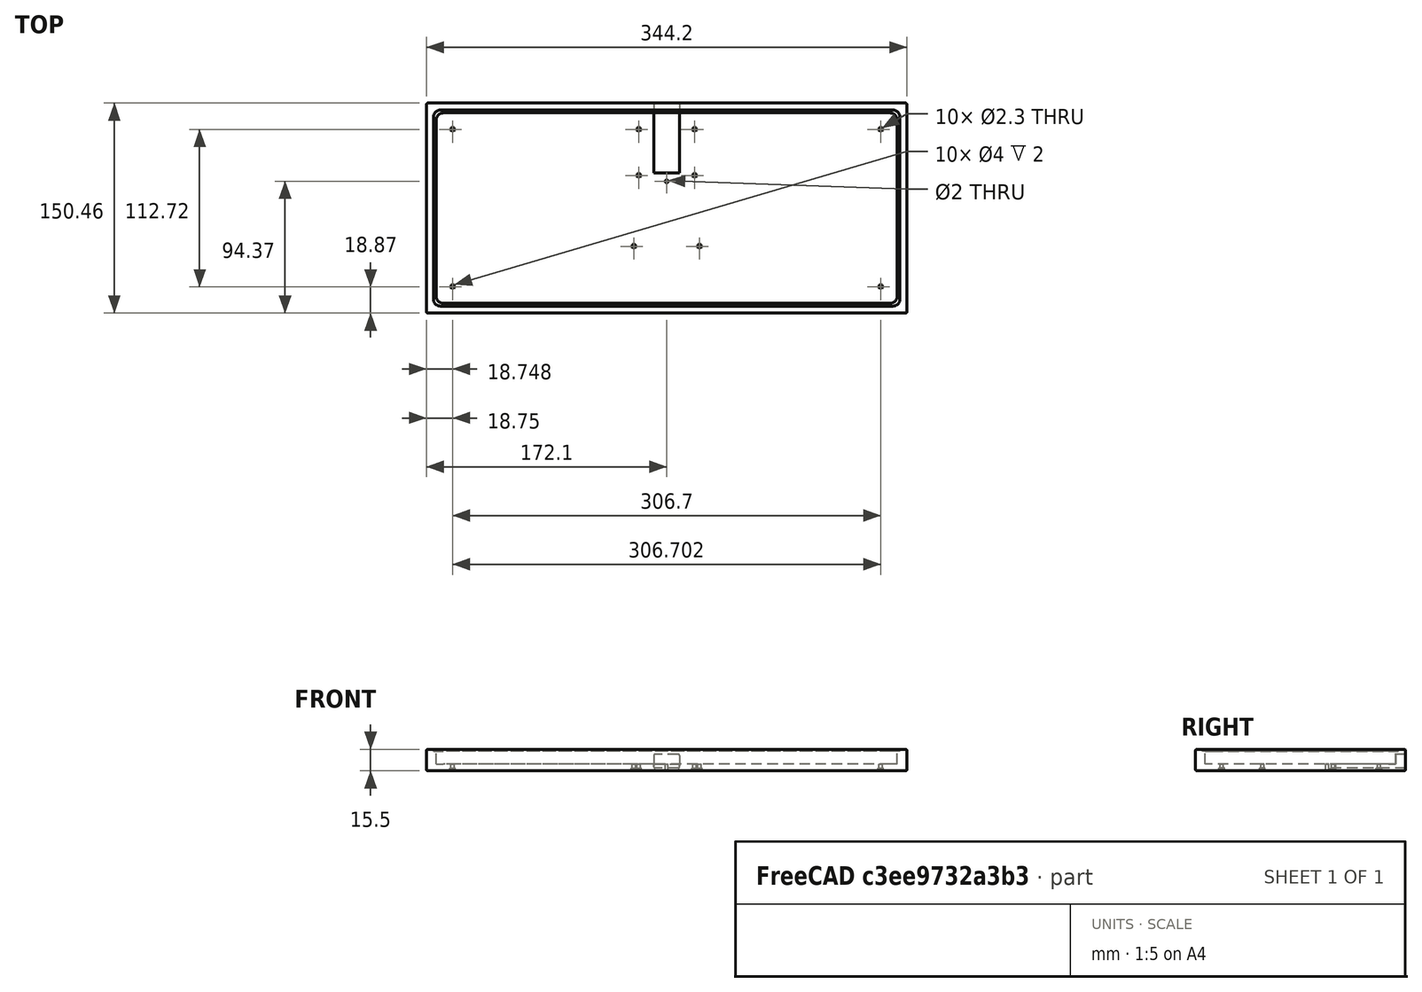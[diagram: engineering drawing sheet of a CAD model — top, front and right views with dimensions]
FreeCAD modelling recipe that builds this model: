
FCSTD DOCUMENT  (FreeCAD 0.18.1R)
Label: bloomer_case
License: All rights reserved
LicenseURL: http://en.wikipedia.org/wiki/All_rights_reserved
objects: Part::Cylinder×21, Part::Cut×6, Part::Box×4, Part::Fillet×4, Part::MultiFuse×2
note: 37 computed .brp shape members not serialized (recipe doc carries the construction recipe); baked Part::Feature solids carry a one-line shape summary decoded from their .brp

FEATURE [Part::Box] Box  label="Cube"
  AttacherType = Attacher::AttachEngine3D
  Height = 10.5
  Length = 330.204
  Placement = pos=(-165.102,-68.23,5) rot=(0,0,1;0rad)
  Width = 136.47
FEATURE [Part::Box] Box001  label="Cube001"
  AttacherType = Attacher::AttachEngine3D
  Height = 1.5
  Length = 334.204
  Placement = pos=(-167.1,-70.23,14) rot=(0,0,1;0rad)
  Width = 140.47
FEATURE [Part::Box] Box002  label="Cube002"
  AttacherType = Attacher::AttachEngine3D
  Height = 15.5
  Length = 344.204
  Placement = pos=(-172.102,-75.235,0) rot=(0,0,1;0rad)
  Width = 150.47
FEATURE [Part::Fillet] Fillet
  Base = -> Box
  Edges = 4 edges r=5: [Edge1,Edge3,Edge5,Edge7]
FEATURE [Part::Fillet] Fillet001
  Base = -> Box001
  Edges = 4 edges r=5: [Edge1,Edge3,Edge5,Edge7]
FEATURE [Part::Cut] Cut
  Base = -> Box002
  Tool = -> Fillet
FEATURE [Part::Cut] Cut001
  Base = -> Cut
  Tool = -> Fillet001
FEATURE [Part::Cylinder] Cylinder
  Angle = 360
  AttacherType = Attacher::AttachEngine3D
  Height = 5
  Placement = pos=(153.35,56.36,0) rot=(0,0,1;0rad)
  Radius = 1.15
FEATURE [Part::Cylinder] Cylinder001
  Angle = 360
  AttacherType = Attacher::AttachEngine3D
  Height = 5
  Placement = pos=(153.35,-56.36,0) rot=(0,0,1;0rad)
  Radius = 1.15
FEATURE [Part::Cylinder] Cylinder002
  Angle = 360
  AttacherType = Attacher::AttachEngine3D
  Height = 5
  Placement = pos=(-153.35,56.36,0) rot=(0,0,1;0rad)
  Radius = 1.15
FEATURE [Part::Cylinder] Cylinder003
  Angle = 360
  AttacherType = Attacher::AttachEngine3D
  Height = 5
  Placement = pos=(-153.35,-56.36,0) rot=(0,0,1;0rad)
  Radius = 1.15
FEATURE [Part::Cylinder] Cylinder004
  Angle = 360
  AttacherType = Attacher::AttachEngine3D
  Height = 5
  Placement = pos=(-20,-56.36,0) rot=(0,0,1;0rad)
  Radius = 1.15
FEATURE [Part::Cylinder] Cylinder005
  Angle = 360
  AttacherType = Attacher::AttachEngine3D
  Height = 5
  Placement = pos=(20,-56.36,0) rot=(0,0,1;0rad)
  Radius = 1.15
FEATURE [Part::Cylinder] Cylinder006
  Angle = 360
  AttacherType = Attacher::AttachEngine3D
  Height = 5
  Placement = pos=(-20,-23.36,0) rot=(0,0,1;0rad)
  Radius = 1.15
FEATURE [Part::Cylinder] Cylinder007
  Angle = 360
  AttacherType = Attacher::AttachEngine3D
  Height = 5
  Placement = pos=(20,-23.36,0) rot=(0,0,1;0rad)
  Radius = 1.15
FEATURE [Part::Cylinder] Cylinder008
  Angle = 360
  AttacherType = Attacher::AttachEngine3D
  Height = 5
  Placement = pos=(-23.5,27.36,0) rot=(0,0,1;0rad)
  Radius = 1.15
FEATURE [Part::Cylinder] Cylinder009
  Angle = 360
  AttacherType = Attacher::AttachEngine3D
  Height = 5
  Placement = pos=(23.5,27.36,0) rot=(0,0,1;0rad)
  Radius = 1.15
FEATURE [Part::MultiFuse] Fusion
  Shapes = -> [Cylinder,Cylinder008,Cylinder006,Cylinder009,Cylinder007,Cylinder001,Cylinder002,Cylinder003,Cylinder004,Cylinder005]
FEATURE [Part::Cut] Cut002
  Base = -> Cut001
  Tool = -> Fusion
FEATURE [Part::Cylinder] Cylinder010
  Angle = 360
  AttacherType = Attacher::AttachEngine3D
  Height = 5
  Placement = pos=(0,-19.14,0) rot=(0,0,1;0rad)
  Radius = 1
FEATURE [Part::Cut] Cut003
  Base = -> Cut002
  Tool = -> Cylinder010
FEATURE [Part::Box] Box003  label="Cube003"
  AttacherType = Attacher::AttachEngine3D
  Height = 10
  Length = 18.5
  Placement = pos=(-9.25,-75.25,2) rot=(0,0,1;0rad)
  Width = 50
FEATURE [Part::Cut] Cut004
  Base = -> Cut003
  Tool = -> Box003
FEATURE [Part::Fillet] Fillet002
  Base = -> Cut004
  Edges = 12 edges r=1: [Edge1,Edge2,Edge3,Edge4,Edge5,Edge6,Edge7,Edge12,Edge13,Edge22,Edge23,Edge24]
FEATURE [Part::Fillet] Fillet003
  Base = -> Fillet002
  Edges = 4 edges r=1: [Edge65,Edge67,Edge71,Edge72]
FEATURE [Part::Cylinder] Cylinder011
  Angle = 360
  AttacherType = Attacher::AttachEngine3D
  Height = 2
  Placement = pos=(-153.35,-56.36,0) rot=(0,0,1;0rad)
  Radius = 2
FEATURE [Part::Cylinder] Cylinder012
  Angle = 360
  AttacherType = Attacher::AttachEngine3D
  Height = 2
  Placement = pos=(-153.35,56.36,0) rot=(0,0,1;0rad)
  Radius = 2
FEATURE [Part::Cylinder] Cylinder013
  Angle = 360
  AttacherType = Attacher::AttachEngine3D
  Height = 2
  Placement = pos=(-20,-23.36,0) rot=(0,0,1;0rad)
  Radius = 2
FEATURE [Part::Cylinder] Cylinder014
  Angle = 360
  AttacherType = Attacher::AttachEngine3D
  Height = 2
  Placement = pos=(-20,-56.36,0) rot=(0,0,1;0rad)
  Radius = 2
FEATURE [Part::Cylinder] Cylinder015
  Angle = 360
  AttacherType = Attacher::AttachEngine3D
  Height = 2
  Placement = pos=(-23.5,27.36,0) rot=(0,0,1;0rad)
  Radius = 2
FEATURE [Part::Cylinder] Cylinder016
  Angle = 360
  AttacherType = Attacher::AttachEngine3D
  Height = 2
  Placement = pos=(23.5,27.36,0) rot=(0,0,1;0rad)
  Radius = 2
FEATURE [Part::Cylinder] Cylinder017
  Angle = 360
  AttacherType = Attacher::AttachEngine3D
  Height = 2
  Placement = pos=(153.352,-56.36,0) rot=(0,0,1;0rad)
  Radius = 2
FEATURE [Part::Cylinder] Cylinder018
  Angle = 360
  AttacherType = Attacher::AttachEngine3D
  Height = 2
  Placement = pos=(153.352,56.36,0) rot=(0,0,1;0rad)
  Radius = 2
FEATURE [Part::Cylinder] Cylinder019
  Angle = 360
  AttacherType = Attacher::AttachEngine3D
  Height = 2
  Placement = pos=(20,-23.36,0) rot=(0,0,1;0rad)
  Radius = 2
FEATURE [Part::Cylinder] Cylinder020
  Angle = 360
  AttacherType = Attacher::AttachEngine3D
  Height = 2
  Placement = pos=(20,-56.36,0) rot=(0,0,1;0rad)
  Radius = 2
FEATURE [Part::MultiFuse] Fusion001
  Shapes = -> [Cylinder011,Cylinder016,Cylinder012,Cylinder015,Cylinder017,Cylinder013,Cylinder014,Cylinder018,Cylinder019,Cylinder020]
FEATURE [Part::Cut] Cut005
  Base = -> Fillet003
  Placement = pos=(0,0,0) rot=(0,0,1;3.14159rad)
  Tool = -> Fusion001
